# Revit family: 306_08de4f2a65374053af1775d1ac7b5c
name_source: partatom
category: Pipe Accessories
units: mm (PartAtom-declared; Revit-internal decimal feet)

## family parameters
Always vertical = Yes
Cut with Voids When Loaded = No
Part Type = Valve - Breaks Into
Round Connector Dimension = Use Diameter
Shared = No
Work Plane-Based = No

## types (3) — shared parameters
B = 42 mm  [stored 0.137795 ft]
C = 52 mm  [stored 0.170604 ft]
CAT0 = Yes
CT2 = 21 mm
Description = Thermostatic mixing valve VTA362, PN10 external thread
L2D = 56 mm
L2D_Min = 3048 mm  [stored 10 ft]
LT2 = 28 mm  [stored 0.0918635 ft]
MC = No
Manufacturer = ESBE
QmdConnectorList = 301;D;302;D
URL = http://www.esbe.eu
W1 = 17 mm  [stored 0.0557743 ft]
WT2 = 23 mm  [stored 0.0754593 ft]
X1 = 2 mm  [stored 0.00656168 ft]
X2 = 7 mm  [stored 0.0229659 ft]
X3 = 52 mm  [stored 0.170604 ft]
X4 = 44 mm  [stored 0.144357 ft]
magiPartTypeId = 306
magiProductFamilyId = 08de4f2a65374053af1775d1ac7b5c

## per-type parameters (varying)
| type | A | A__ve | D | DT2 | R2 | W2D | Z1 | Z1__ve | Z2 | magiProductId |
| VTA362 32-49°C 15-1,2 G3/4 | 30 mm  [stored 0.0984252 ft] | -30 mm  [stored -0.0984252 ft] | 20 mm | 10 mm  [stored 0.0328084 ft] | 9 mm  [stored 0.0295276 ft] | 20 mm  [stored 0.0656168 ft] | 6 mm  [stored 0.019685 ft] | -6 mm | 17 mm  [stored 0.0557743 ft] | 6b6009d23ff94ff48c8b99a49109c8 |
| VTA362 35-60°C 20-1,3 G1 | 32 mm | -32 mm | 25 mm | 13 mm  [stored 0.0426509 ft] | 11 mm  [stored 0.0360892 ft] | 25 mm  [stored 0.082021 ft] | 5 mm  [stored 0.0164042 ft] | -5 mm  [stored -0.0164042 ft] | 15 mm  [stored 0.0492126 ft] | 76b8799a3aaa45e194d9607ddaeace |
| VTA362 35-60°C 15-1,2 G3/4 | 30 mm  [stored 0.0984252 ft] | -30 mm  [stored -0.0984252 ft] | 20 mm | 10 mm  [stored 0.0328084 ft] | 9 mm  [stored 0.0295276 ft] | 20 mm  [stored 0.0656168 ft] | 6 mm  [stored 0.019685 ft] | -6 mm | 17 mm  [stored 0.0557743 ft] | c45f6db3116e42769fd309066e051d |

note: column(s) folded — value = type name in every type: magiProductCode

note: [stored X ft] marks values corroborated as IEEE doubles in the binary element streams (Revit-internal decimal feet)

## geometry (parser evidence)
native form markers: Sweep x1
no freeform markers — native parametric forms only
